# Revit family: CBF
name_source: partatom
category: Mechanical Equipment
units: mm (PartAtom-declared; Revit-internal decimal feet)

## family parameters
Always vertical = Yes
Cut with Voids When Loaded = No
Part Type = Normal
Room Calculation Point = No
Round Connector Dimension = Use Diameter
Shared = No
Work Plane-Based = No

## types (1)
- CBF
    0 = 0"
    1" = 1"
    1.5 = 1 1/2"
    2" = 2"
    2' = 24"
    3" = 3"
    3.5 = 3 1/2"
    4" = 4"
    GRILLE_HEIGHT = 10 9/16"
    GRILLE_HEIGHT/2 = 5 9/32"
    GRILLE_WIDTH = 18 9/16"
    GRILLE_WIDTH/2 = 9 9/32"
    HALF = 1/2"
    HOUSING_HEIGHT = 7 11/16"
    HOUSING_HEIGHT/2 = 3 27/32"
    HOUSING_LENGTH = 11 13/16"
    HOUSING_LENGTH/2 = 5 29/32"
    HOUSING_WIDTH = 15 5/8"
    HOUSING_WIDTH/2 = 7 13/16"
    Manufacturer = Loren Cook Company
    Model = CBF
    ONE EIGTH = 1/8"
    THREE EIGHTHS = 3/8"
    Type Comments = Transfer Fan Thru Wall Mounting Direct Drive
    URL = www.lorencook.com

## geometry (parser evidence)
native form markers: Sweep x2
no freeform markers — native parametric forms only
